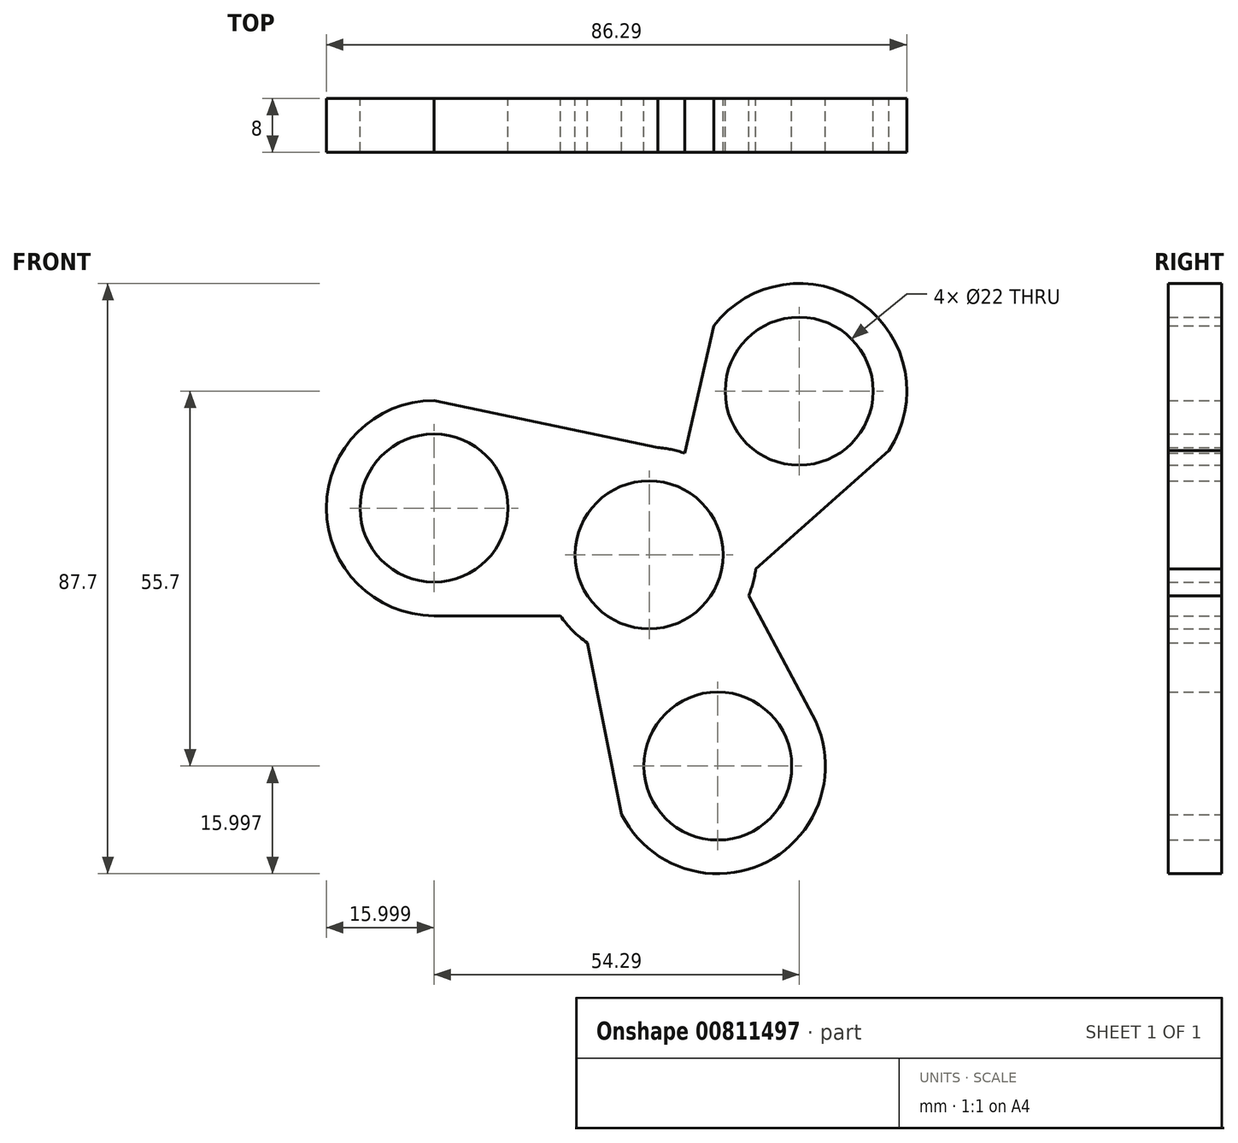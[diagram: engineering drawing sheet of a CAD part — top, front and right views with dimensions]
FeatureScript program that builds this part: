
annotation { "Feature Type Name" : "Feature", "Feature Type Description" : "" }
export const myFeature = defineFeature(function(context is Context, id is Id, definition is map)
    precondition{}
    {
        {
            var Q0;
            Q0=qCreatedBy(makeId("Front.planeOp"),FACE);
            var sketch = newSketch(context, id + "F0", { "sketchPlane" : qUnion([Q0])});
            skCircle(sketch, "E0", {"center": v(22.3, 24.32) * mm, "radius": 11 * mm});
            skCircle(sketch, "E1", {"center": v(10.2, -31.38) * mm, "radius": 11 * mm});
            skCircle(sketch, "E2", {"center": v(-31.98, 6.95) * mm, "radius": 11 * mm});
            skCircle(sketch, "E3", {"center": v(22.3, 24.32) * mm, "radius": 16 * mm});
            skCircle(sketch, "E4", {"center": v(-31.98, 6.95) * mm, "radius": 16 * mm});
            skCircle(sketch, "E5", {"center": v(10.2, -31.38) * mm, "radius": 16 * mm});
            skCircle(sketch, "E6", {"center": v(0, 0) * mm, "radius": 11 * mm});
            skCircle(sketch, "E7", {"center": v(0, 0) * mm, "radius": 16 * mm});
            skLineSegment(sketch, "E8", {"start": v(-31.98, -9.05) * mm, "end": v(-13.2, -9.05) * mm});
            skLineSegment(sketch, "E9", {"start": v(-31.98, 22.95) * mm, "end": v(1.27, 15.95) * mm});
            skLineSegment(sketch, "E10", {"start": v(-4.07, -38.6) * mm, "end": v(-9.2, -13.1) * mm});
            skLineSegment(sketch, "E11", {"start": v(24.3, -23.83) * mm, "end": v(14.8, -6.08) * mm});
            skLineSegment(sketch, "E12", {"start": v(9.59, 34.02) * mm, "end": v(5.27, 15.1) * mm});
            skLineSegment(sketch, "E13", {"start": v(35.66, 15.5) * mm, "end": v(15.86, -2.08) * mm});
            skPoint(sketch, "E14.endSnap0", {"position": v(7.43, 24.56) * mm});
            skSolve(sketch);
        }
        {
            var Q0;
            {var subQ0=sQuery(id+"F0.wireOp",EDGE,"E8");Q0=makeQuery(id+"F0.imprint","IMPRINT",FACE,{"disambiguationData":[TD([[makeQuery(id+"F0.imprint","IMPRINT",EDGE,{"derivedFrom":subQ0}),1.0]])]});}
            var Q1;
            Q1=makeQuery(id+"F0.imprint","IMPRINT",FACE,{"disambiguationData":[TD([[makeQuery(id+"F0.imprint","IMPRINT",EDGE,{"derivedFrom":sQuery(id+"F0.wireOp",EDGE,"E2")}),-1.0]])]});
            var Q2;
            {var subQ0=sQuery(id+"F0.wireOp",EDGE,"E12");var subQ1=sQuery(id+"F0.wireOp",EDGE,"E3");var subQ2=makeQuery(id+"F0.imprint","INTERSECT",VERTEX,{"disambiguationData":[OD(1.0)],"derivedFrom":[subQ1,subQ0]});Q2=makeQuery(id+"F0.imprint","IMPRINT",FACE,{"disambiguationData":[TD([[makeQuery(id+"F0.imprint","IMPRINT",EDGE,{"disambiguationData":[TD([[subQ2,-1.0]])],"derivedFrom":subQ1}),-1.0]])]});}
            var Q3;
            Q3=makeQuery(id+"F0.imprint","IMPRINT",FACE,{"disambiguationData":[TD([[makeQuery(id+"F0.imprint","IMPRINT",EDGE,{"derivedFrom":sQuery(id+"F0.wireOp",EDGE,"E6")}),-1.0]])]});
            var Q4;
            Q4=makeQuery(id+"F0.imprint","IMPRINT",FACE,{"disambiguationData":[TD([[makeQuery(id+"F0.imprint","IMPRINT",EDGE,{"derivedFrom":sQuery(id+"F0.wireOp",EDGE,"E0")}),-1.0]])]});
            var Q5;
            {var subQ0=sQuery(id+"F0.wireOp",EDGE,"E11");Q5=makeQuery(id+"F0.imprint","IMPRINT",FACE,{"disambiguationData":[TD([[makeQuery(id+"F0.imprint","IMPRINT",EDGE,{"derivedFrom":subQ0}),1.0]])]});}
            var Q6;
            Q6=makeQuery(id+"F0.imprint","IMPRINT",FACE,{"disambiguationData":[TD([[makeQuery(id+"F0.imprint","IMPRINT",EDGE,{"derivedFrom":sQuery(id+"F0.wireOp",EDGE,"E1")}),-1.0]])]});
            extrude(context, id + "F1", {"entities" : qUnion([Q0, Q1, Q2, Q3, Q4, Q5, Q6]), "depth" : 8 * mm, "offsetDistance" : 25 * mm});
        }
    });
